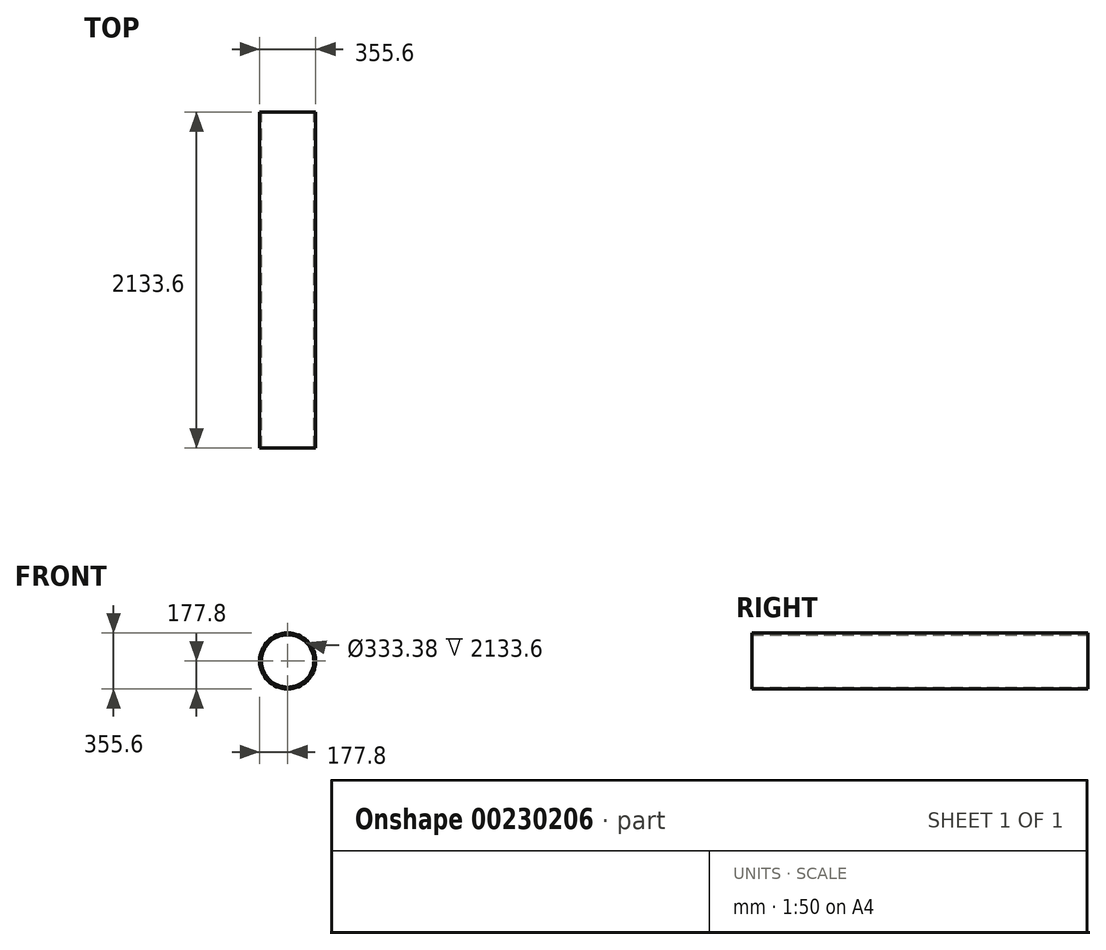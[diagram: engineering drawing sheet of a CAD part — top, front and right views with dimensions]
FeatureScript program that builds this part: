
annotation { "Feature Type Name" : "Feature", "Feature Type Description" : "" }
export const myFeature = defineFeature(function(context is Context, id is Id, definition is map)
    precondition{}
    {
        {
            var Q0;
            Q0=qCreatedBy(makeId("Front.planeOp"),FACE);
            var sketch = newSketch(context, id + "F0", { "sketchPlane" : qUnion([Q0])});
            skCircle(sketch, "E0", {"center": v(0, 0) * mm, "radius": 177.8 * mm});
            skCircle(sketch, "E1", {"center": v(0, 0) * mm, "radius": 166.69 * mm});
            skSolve(sketch);
        }
        {
            var Q0;
            Q0=makeQuery(id+"F0.imprint","IMPRINT",FACE,{"disambiguationData":[TD([[makeQuery(id+"F0.imprint","IMPRINT",EDGE,{"derivedFrom":sQuery(id+"F0.wireOp",EDGE,"E0")}),1.0]])]});
            extrude(context, id + "F1", {"entities" : qUnion([Q0]), "depth" : 2133.6 * mm});
        }
    });
